# Revit family: Lighting_Fixture-Prudential_Lighting-P4000_Semi_recessed
name_source: partatom
category: Lighting Fixtures
revit_build: Autodesk Revit 2015 (Build: 20140606_1530(x64)
units: mm (PartAtom-declared; Revit-internal decimal feet)

## types (60) — shared parameters
Apparent Load = 54 VA
Assembly Code = D5020210
Color Filter = 16777215
Default Elevation = 0' - 0"
Description = Semi-Recessed Direct Lighting
Dimming Lamp Color Temperature Shift = <None>
Emit from Line Length = 2' - 0"
Fixture Rotation = 0.00°
Frequency = 60 Hz
Housing Material = Steel - Prudential Lighting - White
Light Rotation Location = 0' - 0"
Load Classification = Lighting
Manufacturer = Prudential Lighting
Number of Poles = 1
Power Factor = 1
Product Documentation Link = http://www.prulite.com
Product Name = Sky Oculus P4000
Product Page URL = http://www.prulite.com
Shielding Material = Acrylic - Prudential Lighting - White
Tilt Angle = 90.00°
URL = http://www.prulite.com

## per-type parameters (varying)
| type | Lamp | Lamp Quantity | Nominal Diameter | Phase | Photometric Web File | Recessed Kit | Semi Recessed | Total Lumens | Voltage | Wattage Comments |
| P4018-3Bx18w-120V-SMR4 | Biax | 3 | 1' - 6" | 1 | P3918-3BX-WA-D1.IES | 1' - 7 5/8" | 0' - 4" | 1250 lm | 120 V | 18W |
| P4018-3Bx18w-277V-SMR4 | Biax | 3 | 1' - 6" | 2 | P3918-3BX-WA-D1.IES | 1' - 7 5/8" | 0' - 4" | 1250 lm | 277 V | 18W |
| P4018-3Bx18w-347V-SMR4 | Biax | 3 | 1' - 6" | 2 | P3918-3BX-WA-D1.IES | 1' - 7 5/8" | 0' - 4" | 1250 lm | 347 V | 18W |
| P4020-1T8U6-120V-SMR4 | 1T8 | 1 | 2' - 0" | 1 | P3920-1T8U6-WA-D1.IES | 2' - 1 5/8" | 0' - 4" | 2750 lm | 120 V | 18W |
| P4020-1T8U6-277V-SMR4 | 1T8 | 1 | 2' - 0" | 2 | P3920-1T8U6-WA-D1.IES | 2' - 1 5/8" | 0' - 4" | 2750 lm | 277 V | 18W |
| P4020-1T8U6-347V-SMR4 | 1T8 | 1 | 2' - 0" | 2 | P3920-1T8U6-WA-D1.IES | 2' - 1 5/8" | 0' - 4" | 2750 lm | 347 V | 18W |
| P4020-2Bx39w-120V-SMR4 | 1T8 | 2 | 2' - 0" | 1 | P3920-2BX39w-WA-D1.IES | 2' - 1 5/8" | 0' - 4" | 5700 lm | 120 V | 39W |
| P4020-2Bx39w-277V-SMR4 | 1T8 | 2 | 2' - 0" | 2 | P3920-2BX39w-WA-D1.IES | 2' - 1 5/8" | 0' - 4" | 5700 lm | 277 V | 39W |
| P4020-2Bx39w-347V-SMR4 | 1T8 | 2 | 2' - 0" | 2 | P3920-2BX39w-WA-D1.IES | 2' - 1 5/8" | 0' - 4" | 5700 lm | 347 V | 39W |
| P4020-2Bx55w-120V-SMR4 | 1T8 | 2 | 2' - 0" | 1 | P3920-2BX55w-WA-D9.ies | 2' - 1 5/8" | 0' - 4" | 5700 lm | 120 V | 55W |
| P4020-2Bx55w-277V-SMR4 | 1T8 | 2 | 2' - 0" | 2 | P3920-2BX55w-WA-D9.ies | 2' - 1 5/8" | 0' - 4" | 5700 lm | 277 V | 55W |
| P4020-2Bx55w-347V-SMR4 | 1T8 | 2 | 2' - 0" | 2 | P3920-2BX55w-WA-D9.ies | 2' - 1 5/8" | 0' - 4" | 5700 lm | 347 V | 55W |
| P4030-3T8U6-120V-SMR4 | 3T8U6 | 3 | 3' - 0" | 1 | P3930-3T8U6-WA-D1.IES | 3' - 1 5/8" | 0' - 4" | 2850 lm | 120 V | 32W |
| P4030-3T8U6-277V-SMR4 | 3T8U6 | 3 | 3' - 0" | 2 | P3930-3T8U6-WA-D1.IES | 3' - 1 5/8" | 0' - 4" | 2850 lm | 277 V | 32W |
| P4030-3T8U6-347V-SMR4 | 3T8U6 | 3 | 3' - 0" | 2 | P3930-3T8U6-WA-D1.IES | 3' - 1 5/8" | 0' - 4" | 2850 lm | 347 V | 32W |
| P4030-6T5-120V-SMR4 | 6T5 | 6 | 3' - 0" | 1 | P3930-6T5-WA-D9.ies | 3' - 1 5/8" | 0' - 4" | 2850 lm | 120 V | 21W |
| P4030-6T5-277V-SMR4 | 6T5 | 6 | 3' - 0" | 2 | P3930-6T5-WA-D9.ies | 3' - 1 5/8" | 0' - 4" | 2850 lm | 277 V | 21W |
| P4030-6T5-347V-SMR4 | 6T5 | 6 | 3' - 0" | 2 | P3930-6T5-WA-D9.ies | 3' - 1 5/8" | 0' - 4" | 2850 lm | 347 V | 21W |
| P4030-T5HO-120V-SMR4 | T5HO | 6 | 3' - 0" | 1 | P4030-5T5-WA-D1.IES | 3' - 1 5/8" | 0' - 4" | 2850 lm | 120 V | 21W |
| P4030-T5HO-277V-SMR4 | T5HO | 6 | 3' - 0" | 2 | P4030-5T5-WA-D1.IES | 3' - 1 5/8" | 0' - 4" | 2850 lm | 277 V | 21W |
| P4030-T5HO-347V-SMR4 | T5HO | 6 | 3' - 0" | 2 | P4030-5T5-WA-D1.IES | 3' - 1 5/8" | 0' - 4" | 2850 lm | 347 V | 21W |
| P4040-5T8U6-120V-SMR4 | 5T8U6 | 5 | 4' - 0" | 1 | P3940-5T8U6-WA-D1.IES | 4' - 1 5/8" | 0' - 4" | 2850 lm | 120 V | 32W |
| P4040-5T8U6-277V-SMR4 | 5T8U6 | 5 | 4' - 0" | 2 | P3940-5T8U6-WA-D1.IES | 4' - 1 5/8" | 0' - 4" | 2850 lm | 277 V | 32W |
| P4040-5T8U6-347V-SMR4 | 5T8U6 | 5 | 4' - 0" | 2 | P3940-5T8U6-WA-D1.IES | 4' - 1 5/8" | 0' - 4" | 2850 lm | 347 V | 32W |
| P4040-7T5-120V-SMR4 | 7T5 | 7 | 4' - 0" | 1 | P3940-7T5-WA-D1.IES | 4' - 1 5/8" | 0' - 4" | 1700 lm | 120 V | 21W |
| P4040-7T5-277V-SMR4 | 7T5 | 7 | 4' - 0" | 2 | P3940-7T5-WA-D1.IES | 4' - 1 5/8" | 0' - 4" | 1700 lm | 277 V | 21W |
| P4040-7T5-347V-SMR4 | 7T5 | 7 | 4' - 0" | 2 | P3940-7T5-WA-D1.IES | 4' - 1 5/8" | 0' - 4" | 1700 lm | 347 V | 21W |
| P4040-T5HO-120V-SMR4 | T5HO | 6 | 4' - 0" | 1 | P3940-7T5-WA-D1.IES | 4' - 1 5/8" | 0' - 4" | 1700 lm | 120 V | 21W |
| P4040-T5HO-277V-SMR4 | T5HO | 6 | 4' - 0" | 2 | P3940-7T5-WA-D1.IES | 4' - 1 5/8" | 0' - 4" | 1700 lm | 277 V | 21W |
| P4040-T5HO-347V-SMR4 | T5HO | 6 | 4' - 0" | 2 | P3940-7T5-WA-D1.IES | 4' - 1 5/8" | 0' - 4" | 1700 lm | 347 V | 21W |
| P4018-3Bx18w-120V-SMR7 | Biax | 3 | 1' - 6" | 1 | P3918-3BX-WA-D1.IES | 1' - 7 5/8" | 0' - 7" | 1250 lm | 120 V | 18W |
| P4018-3Bx18w-277V-SMR7 | Biax | 3 | 1' - 6" | 2 | P3918-3BX-WA-D1.IES | 1' - 7 5/8" | 0' - 7" | 1250 lm | 277 V | 18W |
| P4018-3Bx18w-347V-SMR7 | Biax | 3 | 1' - 6" | 2 | P3918-3BX-WA-D1.IES | 1' - 7 5/8" | 0' - 7" | 1250 lm | 347 V | 18W |
| P4020-1T8U6-120V-SMR7 | 1T8 | 1 | 2' - 0" | 1 | P3920-1T8U6-WA-D1.IES | 2' - 1 5/8" | 0' - 7" | 2750 lm | 120 V | 18W |
| P4020-1T8U6-277V-SMR7 | 1T8 | 1 | 2' - 0" | 2 | P3920-1T8U6-WA-D1.IES | 2' - 1 5/8" | 0' - 7" | 2750 lm | 277 V | 18W |
| P4020-1T8U6-347V-SMR7 | 1T8 | 1 | 2' - 0" | 2 | P3920-1T8U6-WA-D1.IES | 2' - 1 5/8" | 0' - 7" | 2750 lm | 347 V | 18W |
| P4020-2Bx39w-120V-SMR7 | 1T8 | 2 | 2' - 0" | 1 | P3920-2BX39w-WA-D1.IES | 2' - 1 5/8" | 0' - 7" | 5700 lm | 120 V | 39W |
| P4020-2Bx39w-277V-SMR7 | 1T8 | 2 | 2' - 0" | 2 | P3920-2BX39w-WA-D1.IES | 2' - 1 5/8" | 0' - 7" | 5700 lm | 277 V | 39W |
| P4020-2Bx39w-347V-SMR7 | 1T8 | 2 | 2' - 0" | 2 | P3920-2BX39w-WA-D1.IES | 2' - 1 5/8" | 0' - 7" | 5700 lm | 347 V | 39W |
| P4020-2Bx55w-120V-SMR7 | 1T8 | 2 | 2' - 0" | 1 | P3920-2BX55w-WA-D9.ies | 2' - 1 5/8" | 0' - 7" | 5700 lm | 120 V | 55W |
| P4020-2Bx55w-277V-SMR7 | 1T8 | 2 | 2' - 0" | 2 | P3920-2BX55w-WA-D9.ies | 2' - 1 5/8" | 0' - 7" | 5700 lm | 277 V | 55W |
| P4020-2Bx55w-347V-SMR7 | 1T8 | 2 | 2' - 0" | 2 | P3920-2BX55w-WA-D9.ies | 2' - 1 5/8" | 0' - 7" | 5700 lm | 347 V | 55W |
| P4030-3T8U6-120V-SMR7 | 3T8U6 | 3 | 3' - 0" | 1 | P3930-3T8U6-WA-D1.IES | 3' - 1 5/8" | 0' - 7" | 2850 lm | 120 V | 32W |
| P4030-3T8U6-277V-SMR7 | 3T8U6 | 3 | 3' - 0" | 2 | P3930-3T8U6-WA-D1.IES | 3' - 1 5/8" | 0' - 7" | 2850 lm | 277 V | 32W |
| P4030-3T8U6-347V-SMR7 | 3T8U6 | 3 | 3' - 0" | 2 | P3930-3T8U6-WA-D1.IES | 3' - 1 5/8" | 0' - 7" | 2850 lm | 347 V | 32W |
| P4030-6T5-120V-SMR7 | 6T5 | 6 | 3' - 0" | 1 | P3930-6T5-WA-D9.ies | 3' - 1 5/8" | 0' - 7" | 2850 lm | 120 V | 21W |
| P4030-6T5-277V-SMR7 | 6T5 | 6 | 3' - 0" | 2 | P3930-6T5-WA-D9.ies | 3' - 1 5/8" | 0' - 7" | 2850 lm | 277 V | 21W |
| P4030-6T5-347V-SMR7 | 6T5 | 6 | 3' - 0" | 2 | P3930-6T5-WA-D9.ies | 3' - 1 5/8" | 0' - 7" | 2850 lm | 347 V | 21W |
| P4030-T5HO-120V-SMR7 | T5HO | 6 | 3' - 0" | 1 | P4030-5T5-WA-D1.IES | 3' - 1 5/8" | 0' - 7" | 2850 lm | 120 V | 21W |
| P4030-T5HO-277V-SMR7 | T5HO | 6 | 3' - 0" | 2 | P4030-5T5-WA-D1.IES | 3' - 1 5/8" | 0' - 7" | 2850 lm | 277 V | 21W |
| P4030-T5HO-347V-SMR7 | T5HO | 6 | 3' - 0" | 2 | P4030-5T5-WA-D1.IES | 3' - 1 5/8" | 0' - 7" | 2850 lm | 347 V | 21W |
| P4040-5T8U6-120V-SMR7 | 5T8U6 | 5 | 4' - 0" | 1 | P3940-5T8U6-WA-D1.IES | 4' - 1 5/8" | 0' - 7" | 2850 lm | 120 V | 32W |
| P4040-5T8U6-277V-SMR7 | 5T8U6 | 5 | 4' - 0" | 2 | P3940-5T8U6-WA-D1.IES | 4' - 1 5/8" | 0' - 7" | 2850 lm | 277 V | 32W |
| P4040-5T8U6-347V-SMR7 | 5T8U6 | 5 | 4' - 0" | 2 | P3940-5T8U6-WA-D1.IES | 4' - 1 5/8" | 0' - 7" | 2850 lm | 347 V | 32W |
| P4040-7T5-120V-SMR7 | 7T5 | 7 | 4' - 0" | 1 | P3940-7T5-WA-D1.IES | 4' - 1 5/8" | 0' - 7" | 1700 lm | 120 V | 21W |
| P4040-7T5-277V-SMR7 | 7T5 | 7 | 4' - 0" | 2 | P3940-7T5-WA-D1.IES | 4' - 1 5/8" | 0' - 7" | 1700 lm | 277 V | 21W |
| P4040-7T5-347V-SMR7 | 7T5 | 7 | 4' - 0" | 2 | P3940-7T5-WA-D1.IES | 4' - 1 5/8" | 0' - 7" | 1700 lm | 347 V | 21W |
| P4040-T5HO-120V-SMR7 | T5HO | 6 | 4' - 0" | 1 | P3940-7T5-WA-D1.IES | 4' - 1 5/8" | 0' - 7" | 1700 lm | 120 V | 21W |
| P4040-T5HO-277V-SMR7 | T5HO | 6 | 4' - 0" | 2 | P3940-7T5-WA-D1.IES | 4' - 1 5/8" | 0' - 7" | 1700 lm | 277 V | 21W |
| P4040-T5HO-347V-SMR7 | T5HO | 6 | 4' - 0" | 2 | P3940-7T5-WA-D1.IES | 4' - 1 5/8" | 0' - 7" | 1700 lm | 347 V | 21W |

note: column(s) folded — value = type name in every type: Model

## geometry (parser evidence)
native form markers: Sweep x8
no freeform markers — native parametric forms only
